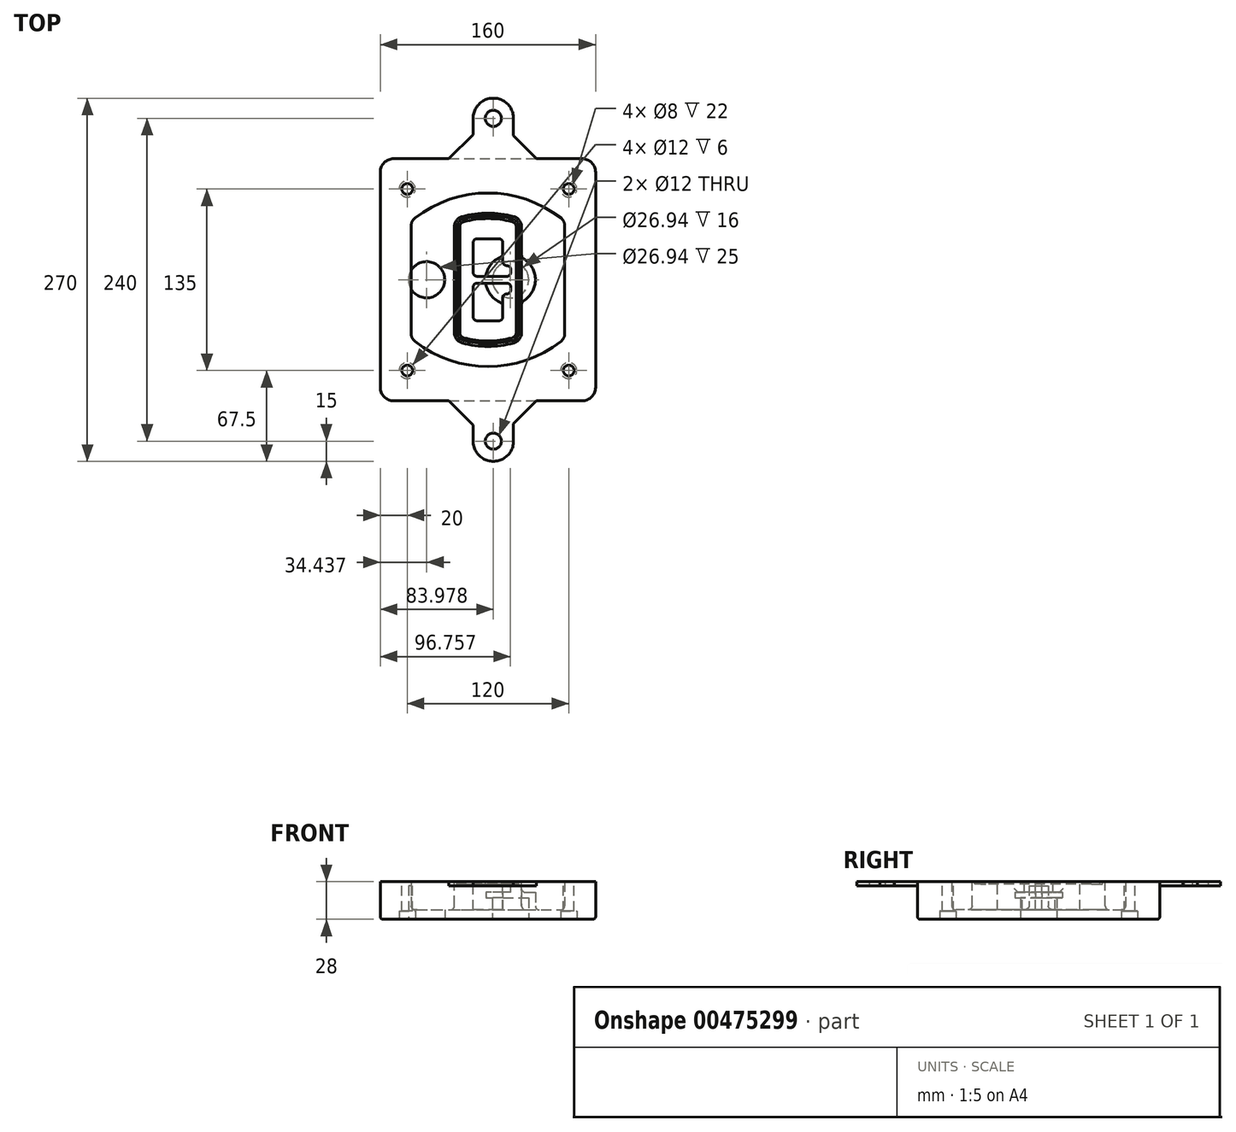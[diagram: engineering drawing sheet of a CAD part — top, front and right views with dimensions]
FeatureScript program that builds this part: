
annotation { "Feature Type Name" : "Feature", "Feature Type Description" : "" }
export const myFeature = defineFeature(function(context is Context, id is Id, definition is map)
    precondition{}
    {
        {
            var Q0;
            Q0=qCreatedBy(makeId("Top.planeOp"),FACE);
            var sketch = newSketch(context, id + "F0", { "sketchPlane" : qUnion([Q0])});
            skPoint(sketch, "E0.rect.middle", {"position": v(0, 0) * mm});
            skLineSegment(sketch, "E1.bottom", {"start": v(-70, -90) * mm, "end": v(70, -90) * mm});
            skLineSegment(sketch, "E1.top", {"start": v(-70, 90) * mm, "end": v(70, 90) * mm});
            skLineSegment(sketch, "E1.left", {"start": v(-80, -80) * mm, "end": v(-80, 80) * mm});
            skLineSegment(sketch, "E1.right", {"start": v(80, -80) * mm, "end": v(80, 80) * mm});
            skLineSegment(sketch, "E2", {"start": v(-80, 90) * mm, "end": v(80, -90) * mm, "construction": true});
            skLineSegment(sketch, "E3", {"start": v(80, 90) * mm, "end": v(-80, -90) * mm, "construction": true});
            skCircle(sketch, "E4", {"center": v(-60, 67.5) * mm, "radius": 4 * mm});
            skCircle(sketch, "E5", {"center": v(60, 67.5) * mm, "radius": 4 * mm});
            skCircle(sketch, "E6", {"center": v(60, -67.5) * mm, "radius": 4 * mm});
            skCircle(sketch, "E7", {"center": v(-60, -67.5) * mm, "radius": 4 * mm});
            skLineSegment(sketch, "E8", {"start": v(-60, 67.5) * mm, "end": v(60, 67.5) * mm, "construction": true});
            skLineSegment(sketch, "E9", {"start": v(60, 67.5) * mm, "end": v(60, -67.5) * mm, "construction": true});
            skLineSegment(sketch, "E10", {"start": v(60, -67.5) * mm, "end": v(-60, -67.5) * mm, "construction": true});
            skLineSegment(sketch, "E11", {"start": v(-60, -67.5) * mm, "end": v(-60, 67.5) * mm, "construction": true});
            skLineSegment(sketch, "E12", {"start": v(-60, 40.3) * mm, "end": v(-60, -40.3) * mm});
            skLineSegment(sketch, "E13", {"start": v(60, 40.3) * mm, "end": v(60, -40.3) * mm});
            skArc(sketch, "E14", {"start": v(56.15, 48.18) * mm, "mid": v(0, 67.5) * mm, "end": v(-56.15, 48.18) * mm});
            skArc(sketch, "E15", {"start": v(-56.15, -48.18) * mm, "mid": v(0, -67.5) * mm, "end": v(56.15, -48.18) * mm});
            skLineSegment(sketch, "E16", {"start": v(-60, 0) * mm, "end": v(60, 0) * mm, "construction": true});
            skPoint(sketch, "E17.visualSharp", {"position": v(-60, -45) * mm});
            skArc(sketch, "E17.filletArc", {"start": v(-60, -40.3) * mm, "mid": v(-58.99, -44.68) * mm, "end": v(-56.15, -48.18) * mm});
            skPoint(sketch, "E18.visualSharp", {"position": v(-60, 45) * mm});
            skArc(sketch, "E18.filletArc", {"start": v(-56.15, 48.18) * mm, "mid": v(-58.99, 44.68) * mm, "end": v(-60, 40.3) * mm});
            skPoint(sketch, "E19.visualSharp", {"position": v(60, 45) * mm});
            skArc(sketch, "E19.filletArc", {"start": v(60, 40.3) * mm, "mid": v(58.99, 44.68) * mm, "end": v(56.15, 48.18) * mm});
            skPoint(sketch, "E20.visualSharp", {"position": v(60, -45) * mm});
            skArc(sketch, "E20.filletArc", {"start": v(56.15, -48.18) * mm, "mid": v(58.99, -44.68) * mm, "end": v(60, -40.3) * mm});
            skPoint(sketch, "E21.visualSharp", {"position": v(-80, 90) * mm});
            skArc(sketch, "E21.filletArc", {"start": v(-70, 90) * mm, "mid": v(-77.07, 87.07) * mm, "end": v(-80, 80) * mm});
            skPoint(sketch, "E22.visualSharp", {"position": v(80, 90) * mm});
            skArc(sketch, "E22.filletArc", {"start": v(80, 80) * mm, "mid": v(77.07, 87.07) * mm, "end": v(70, 90) * mm});
            skPoint(sketch, "E23.visualSharp", {"position": v(80, -90) * mm});
            skArc(sketch, "E23.filletArc", {"start": v(70, -90) * mm, "mid": v(77.07, -87.07) * mm, "end": v(80, -80) * mm});
            skPoint(sketch, "E24.visualSharp", {"position": v(-80, -90) * mm});
            skArc(sketch, "E24.filletArc", {"start": v(-80, -80) * mm, "mid": v(-77.07, -87.07) * mm, "end": v(-70, -90) * mm});
            skArc(sketch, "E25.0", {"start": v(57, 40.3) * mm, "mid": v(56.3, 43.36) * mm, "end": v(54.3, 45.81) * mm});
            skLineSegment(sketch, "E25.1", {"start": v(57, 40.3) * mm, "end": v(57, -40.3) * mm});
            skArc(sketch, "E25.2", {"start": v(54.3, -45.81) * mm, "mid": v(56.3, -43.36) * mm, "end": v(57, -40.3) * mm});
            skArc(sketch, "E25.3", {"start": v(-54.3, -45.81) * mm, "mid": v(0, -64.5) * mm, "end": v(54.3, -45.81) * mm});
            skArc(sketch, "E25.4", {"start": v(-57, -40.3) * mm, "mid": v(-56.3, -43.36) * mm, "end": v(-54.3, -45.81) * mm});
            skArc(sketch, "E25.5", {"start": v(54.3, 45.81) * mm, "mid": v(0, 64.5) * mm, "end": v(-54.3, 45.81) * mm});
            skLineSegment(sketch, "E25.6", {"start": v(-57, 40.3) * mm, "end": v(-57, -40.3) * mm});
            skArc(sketch, "E25.7", {"start": v(-54.3, 45.81) * mm, "mid": v(-56.3, 43.36) * mm, "end": v(-57, 40.3) * mm});
            skArc(sketch, "E26.0", {"start": v(-58.62, 51.33) * mm, "mid": v(-62.58, 46.43) * mm, "end": v(-64, 40.3) * mm});
            skArc(sketch, "E26.1", {"start": v(58.62, 51.33) * mm, "mid": v(0, 71.5) * mm, "end": v(-58.62, 51.33) * mm});
            skArc(sketch, "E26.2", {"start": v(64, 40.3) * mm, "mid": v(62.58, 46.43) * mm, "end": v(58.62, 51.33) * mm});
            skLineSegment(sketch, "E26.3", {"start": v(64, 40.3) * mm, "end": v(64, -40.3) * mm});
            skArc(sketch, "E26.4", {"start": v(58.62, -51.33) * mm, "mid": v(62.58, -46.43) * mm, "end": v(64, -40.3) * mm});
            skLineSegment(sketch, "E26.5", {"start": v(-64, 40.3) * mm, "end": v(-64, -40.3) * mm});
            skArc(sketch, "E26.6", {"start": v(-58.62, -51.33) * mm, "mid": v(0, -71.5) * mm, "end": v(58.62, -51.33) * mm});
            skArc(sketch, "E26.7", {"start": v(-64, -40.3) * mm, "mid": v(-62.58, -46.43) * mm, "end": v(-58.62, -51.33) * mm});
            skSolve(sketch);
        }
        {
            var Q0;
            Q0=makeQuery(id+"F0.imprint","IMPRINT",FACE,{"disambiguationData":[TD([[makeQuery(id+"F0.imprint","IMPRINT",EDGE,{"derivedFrom":sQuery(id+"F0.wireOp",EDGE,"E1.bottom")}),1.0]])]});
            var Q1;
            Q1=makeQuery(id+"F0.imprint","IMPRINT",FACE,{"disambiguationData":[TD([[makeQuery(id+"F0.imprint","IMPRINT",EDGE,{"derivedFrom":sQuery(id+"F0.wireOp",EDGE,"E12")}),1.0]])]});
            var Q2;
            Q2=makeQuery(id+"F0.imprint","IMPRINT",FACE,{"disambiguationData":[TD([[makeQuery(id+"F0.imprint","IMPRINT",EDGE,{"derivedFrom":sQuery(id+"F0.wireOp",EDGE,"E25.0")}),1.0]])]});
            var Q3;
            Q3=makeQuery(id+"F0.imprint","IMPRINT",FACE,{"disambiguationData":[TD([[makeQuery(id+"F0.imprint","IMPRINT",EDGE,{"derivedFrom":sQuery(id+"F0.wireOp",EDGE,"E12")}),-1.0]])]});
            extrude(context, id + "F1", {"entities" : qUnion([Q0, Q1, Q2, Q3]), "oppositeDirection" : true, "depth" : 25 * mm});
        }
        {
            var Q0;
            Q0=makeQuery(id+"F0.imprint","IMPRINT",FACE,{"disambiguationData":[TD([[makeQuery(id+"F0.imprint","IMPRINT",EDGE,{"derivedFrom":sQuery(id+"F0.wireOp",EDGE,"E12")}),1.0]])]});
            extrude(context, id + "F2", {"entities" : qUnion([Q0]), "operationType" : NewBodyOperationType.ADD, "depth" : 3 * mm});
        }
        {
            var Q0;
            Q0=makeQuery(id+"F0.imprint","IMPRINT",FACE,{"disambiguationData":[TD([[makeQuery(id+"F0.imprint","IMPRINT",EDGE,{"derivedFrom":sQuery(id+"F0.wireOp",EDGE,"E25.0")}),1.0]])]});
            extrude(context, id + "F3", {"entities" : qUnion([Q0]), "operationType" : NewBodyOperationType.REMOVE, "oppositeDirection" : true, "depth" : 18 * mm});
        }
        {
            var Q0;
            Q0=makeQuery(id+"F2.opExtrude","CAP_FACE",FACE,{"disambiguationData":[OSD([sQuery(id+"F0.wireOp",EDGE,"E12"),sQuery(id+"F0.wireOp",EDGE,"E13"),sQuery(id+"F0.wireOp",EDGE,"E14"),sQuery(id+"F0.wireOp",EDGE,"E15"),sQuery(id+"F0.wireOp",EDGE,"E17.filletArc"),sQuery(id+"F0.wireOp",EDGE,"E18.filletArc"),sQuery(id+"F0.wireOp",EDGE,"E19.filletArc"),sQuery(id+"F0.wireOp",EDGE,"E20.filletArc"),sQuery(id+"F0.wireOp",EDGE,"E25.0"),sQuery(id+"F0.wireOp",EDGE,"E25.1"),sQuery(id+"F0.wireOp",EDGE,"E25.2"),sQuery(id+"F0.wireOp",EDGE,"E25.3"),sQuery(id+"F0.wireOp",EDGE,"E25.4"),sQuery(id+"F0.wireOp",EDGE,"E25.5"),sQuery(id+"F0.wireOp",EDGE,"E25.6"),sQuery(id+"F0.wireOp",EDGE,"E25.7")])],"isStart":false});
            var sketch = newSketch(context, id + "F4", { "sketchPlane" : qUnion([Q0])});
            skArc(sketch, "E27.0", {"start": v(-19.08, -46.97) * mm, "mid": v(0, -49.5) * mm, "end": v(19.08, -46.97) * mm});
            skArc(sketch, "E28.0", {"start": v(19.08, 46.97) * mm, "mid": v(0, 49.5) * mm, "end": v(-19.08, 46.97) * mm});
            skLineSegment(sketch, "E29", {"start": v(-25, 39.25) * mm, "end": v(-25, -39.25) * mm});
            skLineSegment(sketch, "E30", {"start": v(25, 39.25) * mm, "end": v(25, -39.25) * mm});
            skLineSegment(sketch, "E31", {"start": v(-25, 45.1) * mm, "end": v(25, 45.1) * mm, "construction": true});
            skLineSegment(sketch, "E32", {"start": v(-25, -45.1) * mm, "end": v(25, -45.1) * mm, "construction": true});
            skPoint(sketch, "E33.visualSharp", {"position": v(-25, 45.1) * mm});
            skArc(sketch, "E33.filletArc", {"start": v(-19.08, 46.97) * mm, "mid": v(-23.35, 44.11) * mm, "end": v(-25, 39.25) * mm});
            skPoint(sketch, "E34.visualSharp", {"position": v(25, 45.1) * mm});
            skArc(sketch, "E34.filletArc", {"start": v(25, 39.25) * mm, "mid": v(23.35, 44.11) * mm, "end": v(19.08, 46.97) * mm});
            skPoint(sketch, "E35.visualSharp", {"position": v(25, -45.1) * mm});
            skArc(sketch, "E35.filletArc", {"start": v(19.08, -46.97) * mm, "mid": v(23.35, -44.11) * mm, "end": v(25, -39.25) * mm});
            skPoint(sketch, "E36.visualSharp", {"position": v(-25, -45.1) * mm});
            skArc(sketch, "E36.filletArc", {"start": v(-25, -39.25) * mm, "mid": v(-23.35, -44.11) * mm, "end": v(-19.08, -46.97) * mm});
            skArc(sketch, "E37.0", {"start": v(54.3, 45.81) * mm, "mid": v(0, 64.5) * mm, "end": v(-54.3, 45.81) * mm});
            skArc(sketch, "E37.1", {"start": v(-54.3, 45.81) * mm, "mid": v(-56.3, 43.36) * mm, "end": v(-57, 40.3) * mm});
            skLineSegment(sketch, "E37.2", {"start": v(-57, 40.3) * mm, "end": v(-57, -40.3) * mm});
            skArc(sketch, "E37.3", {"start": v(-57, -40.3) * mm, "mid": v(-56.3, -43.36) * mm, "end": v(-54.3, -45.81) * mm});
            skArc(sketch, "E37.4", {"start": v(-54.3, -45.81) * mm, "mid": v(0, -64.5) * mm, "end": v(54.3, -45.81) * mm});
            skArc(sketch, "E37.5", {"start": v(54.3, -45.81) * mm, "mid": v(56.3, -43.36) * mm, "end": v(57, -40.3) * mm});
            skLineSegment(sketch, "E37.6", {"start": v(57, 40.3) * mm, "end": v(57, -40.3) * mm});
            skArc(sketch, "E37.7", {"start": v(57, 40.3) * mm, "mid": v(56.3, 43.36) * mm, "end": v(54.3, 45.81) * mm});
            skLineSegment(sketch, "E38.0", {"start": v(23, 39.25) * mm, "end": v(23, -39.25) * mm});
            skArc(sketch, "E38.1", {"start": v(18.56, -45.04) * mm, "mid": v(21.76, -42.9) * mm, "end": v(23, -39.25) * mm});
            skArc(sketch, "E38.2", {"start": v(-18.56, -45.04) * mm, "mid": v(0, -47.5) * mm, "end": v(18.56, -45.04) * mm});
            skArc(sketch, "E38.3", {"start": v(-23, -39.25) * mm, "mid": v(-21.76, -42.9) * mm, "end": v(-18.56, -45.04) * mm});
            skLineSegment(sketch, "E38.4", {"start": v(-23, 39.25) * mm, "end": v(-23, -39.25) * mm});
            skArc(sketch, "E38.5", {"start": v(23, 39.25) * mm, "mid": v(21.76, 42.9) * mm, "end": v(18.56, 45.04) * mm});
            skArc(sketch, "E38.6", {"start": v(-18.56, 45.04) * mm, "mid": v(-21.76, 42.9) * mm, "end": v(-23, 39.25) * mm});
            skArc(sketch, "E38.7", {"start": v(18.56, 45.04) * mm, "mid": v(0, 47.5) * mm, "end": v(-18.56, 45.04) * mm});
            skArc(sketch, "E39.0", {"start": v(21, 39.25) * mm, "mid": v(20.18, 41.68) * mm, "end": v(18.04, 43.1) * mm});
            skLineSegment(sketch, "E39.1", {"start": v(21, 39.25) * mm, "end": v(21, -39.25) * mm});
            skArc(sketch, "E39.2", {"start": v(18.04, -43.1) * mm, "mid": v(20.18, -41.68) * mm, "end": v(21, -39.25) * mm});
            skArc(sketch, "E39.3", {"start": v(-18.04, -43.1) * mm, "mid": v(0, -45.5) * mm, "end": v(18.04, -43.1) * mm});
            skArc(sketch, "E39.4", {"start": v(-21, -39.25) * mm, "mid": v(-20.18, -41.68) * mm, "end": v(-18.04, -43.1) * mm});
            skArc(sketch, "E39.5", {"start": v(18.04, 43.1) * mm, "mid": v(0, 45.5) * mm, "end": v(-18.04, 43.1) * mm});
            skLineSegment(sketch, "E39.6", {"start": v(-21, 39.25) * mm, "end": v(-21, -39.25) * mm});
            skArc(sketch, "E39.7", {"start": v(-18.04, 43.1) * mm, "mid": v(-20.18, 41.68) * mm, "end": v(-21, 39.25) * mm});
            skLineSegment(sketch, "E40", {"start": v(-25, 0) * mm, "end": v(25, 0) * mm, "construction": true});
            skLineSegment(sketch, "E41", {"start": v(-11, 5.5) * mm, "end": v(-11, 27.5) * mm});
            skLineSegment(sketch, "E42", {"start": v(-8, 30.5) * mm, "end": v(8, 30.5) * mm});
            skLineSegment(sketch, "E43", {"start": v(11, 27.5) * mm, "end": v(11, 13.5) * mm});
            skLineSegment(sketch, "E44", {"start": v(14, 10.5) * mm, "end": v(14, 10.5) * mm});
            skLineSegment(sketch, "E45", {"start": v(17, 7.5) * mm, "end": v(17, 5.5) * mm});
            skLineSegment(sketch, "E46", {"start": v(14, 2.5) * mm, "end": v(-8, 2.5) * mm});
            skPoint(sketch, "E47.visualSharp", {"position": v(-11, 30.5) * mm});
            skArc(sketch, "E47.filletArc", {"start": v(-8, 30.5) * mm, "mid": v(-10.12, 29.62) * mm, "end": v(-11, 27.5) * mm});
            skPoint(sketch, "E48.visualSharp", {"position": v(11, 30.5) * mm});
            skArc(sketch, "E48.filletArc", {"start": v(11, 27.5) * mm, "mid": v(10.12, 29.62) * mm, "end": v(8, 30.5) * mm});
            skPoint(sketch, "E49.visualSharp", {"position": v(11, 10.5) * mm});
            skArc(sketch, "E49.filletArc", {"start": v(11, 13.5) * mm, "mid": v(11.88, 11.38) * mm, "end": v(14, 10.5) * mm});
            skPoint(sketch, "E50.visualSharp", {"position": v(17, 10.5) * mm});
            skArc(sketch, "E50.filletArc", {"start": v(17, 7.5) * mm, "mid": v(16.12, 9.62) * mm, "end": v(14, 10.5) * mm});
            skPoint(sketch, "E51.visualSharp", {"position": v(17, 2.5) * mm});
            skArc(sketch, "E51.filletArc", {"start": v(14, 2.5) * mm, "mid": v(16.12, 3.38) * mm, "end": v(17, 5.5) * mm});
            skPoint(sketch, "E52.visualSharp", {"position": v(-11, 2.5) * mm});
            skArc(sketch, "E52.filletArc", {"start": v(-11, 5.5) * mm, "mid": v(-10.12, 3.38) * mm, "end": v(-8, 2.5) * mm});
            skLineSegment(sketch, "E53.0.MirrorCS", {"start": v(14, -2.5) * mm, "end": v(-8, -2.5) * mm});
            skArc(sketch, "E54.0.MirrorCS", {"start": v(-11, -5.5) * mm, "mid": v(-10.12, -3.38) * mm, "end": v(-8, -2.5) * mm});
            skLineSegment(sketch, "E55.0.MirrorCS", {"start": v(-11, -5.5) * mm, "end": v(-11, -27.5) * mm});
            skArc(sketch, "E56.0.MirrorCS", {"start": v(-8, -30.5) * mm, "mid": v(-10.12, -29.62) * mm, "end": v(-11, -27.5) * mm});
            skLineSegment(sketch, "E57.0.MirrorCS", {"start": v(-8, -30.5) * mm, "end": v(8, -30.5) * mm});
            skArc(sketch, "E58.0.MirrorCS", {"start": v(11, -27.5) * mm, "mid": v(10.12, -29.62) * mm, "end": v(8, -30.5) * mm});
            skLineSegment(sketch, "E59.0.MirrorCS", {"start": v(11, -27.5) * mm, "end": v(11, -13.5) * mm});
            skArc(sketch, "E60.0.MirrorCS", {"start": v(11, -13.5) * mm, "mid": v(11.88, -11.38) * mm, "end": v(14, -10.5) * mm});
            skArc(sketch, "E61.0.MirrorCS", {"start": v(17, -7.5) * mm, "mid": v(16.12, -9.62) * mm, "end": v(14, -10.5) * mm});
            skLineSegment(sketch, "E62.0.MirrorCS", {"start": v(17, -7.5) * mm, "end": v(17, -5.5) * mm});
            skArc(sketch, "E63.0.MirrorCS", {"start": v(14, -2.5) * mm, "mid": v(16.12, -3.38) * mm, "end": v(17, -5.5) * mm});
            skSolve(sketch);
        }
        {
            var Q0;
            Q0=makeQuery(id+"F4.imprint","IMPRINT",FACE,{"disambiguationData":[TD([[makeQuery(id+"F4.imprint","IMPRINT",EDGE,{"derivedFrom":sQuery(id+"F4.wireOp",EDGE,"E27.0")}),1.0]])]});
            var Q1;
            Q1=makeQuery(id+"F4.imprint","IMPRINT",FACE,{"disambiguationData":[TD([[makeQuery(id+"F4.imprint","IMPRINT",EDGE,{"derivedFrom":sQuery(id+"F4.wireOp",EDGE,"E38.0")}),-1.0]])]});
            var Q2;
            Q2=makeQuery(id+"F4.imprint","IMPRINT",FACE,{"disambiguationData":[TD([[makeQuery(id+"F4.imprint","IMPRINT",EDGE,{"derivedFrom":sQuery(id+"F4.wireOp",EDGE,"E39.0")}),1.0]])]});
            extrude(context, id + "F5", {"entities" : qUnion([Q0, Q1, Q2]), "operationType" : NewBodyOperationType.ADD, "endBound" : BoundingType.UP_TO_NEXT, "oppositeDirection" : true, "depth" : 25 * mm});
        }
        {
            var Q0;
            Q0=makeQuery(id+"F4.imprint","IMPRINT",FACE,{"disambiguationData":[TD([[makeQuery(id+"F4.imprint","IMPRINT",EDGE,{"derivedFrom":sQuery(id+"F4.wireOp",EDGE,"E38.0")}),-1.0]])]});
            extrude(context, id + "F6", {"entities" : qUnion([Q0]), "operationType" : NewBodyOperationType.REMOVE, "oppositeDirection" : true, "depth" : 2 * mm});
        }
        {
            var Q0;
            Q0=makeQuery(id+"F1.opExtrude","CAP_FACE",FACE,{"disambiguationData":[OSD([sQuery(id+"F0.wireOp",EDGE,"E1.bottom"),sQuery(id+"F0.wireOp",EDGE,"E1.top"),sQuery(id+"F0.wireOp",EDGE,"E1.left"),sQuery(id+"F0.wireOp",EDGE,"E1.right"),sQuery(id+"F0.wireOp",EDGE,"E4"),sQuery(id+"F0.wireOp",EDGE,"E5"),sQuery(id+"F0.wireOp",EDGE,"E6"),sQuery(id+"F0.wireOp",EDGE,"E7"),sQuery(id+"F0.wireOp",EDGE,"E21.filletArc"),sQuery(id+"F0.wireOp",EDGE,"E22.filletArc"),sQuery(id+"F0.wireOp",EDGE,"E23.filletArc"),sQuery(id+"F0.wireOp",EDGE,"E24.filletArc")])],"isStart":false});
            var sketch = newSketch(context, id + "F7", { "sketchPlane" : qUnion([Q0])});
            skCircle(sketch, "E64", {"center": v(16.76, 0) * mm, "radius": 13.47 * mm});
            skCircle(sketch, "E65", {"center": v(-45.56, 0) * mm, "radius": 13.47 * mm});
            skLineSegment(sketch, "E66", {"start": v(80, 0) * mm, "end": v(-80, 0) * mm});
            skCircle(sketch, "E67", {"center": v(16.76, 0) * mm, "radius": 18.47 * mm});
            skCircle(sketch, "E68", {"center": v(60, -67.5) * mm, "radius": 6 * mm});
            skCircle(sketch, "E69", {"center": v(-60, -67.5) * mm, "radius": 6 * mm});
            skCircle(sketch, "E70", {"center": v(-60, 67.5) * mm, "radius": 6 * mm});
            skCircle(sketch, "E71", {"center": v(60, 67.5) * mm, "radius": 6 * mm});
            skSolve(sketch);
        }
        {
            var Q0;
            {var subQ1=sQuery(id+"F7.wireOp",EDGE,"E66");var subQ4=sQuery(id+"F7.wireOp",EDGE,"E64");var subQ6=makeQuery(id+"F7.imprint","INTERSECT",VERTEX,{"disambiguationData":[OD(0.0)],"derivedFrom":[subQ4,subQ1]});Q0=makeQuery(id+"F7.imprint","IMPRINT",FACE,{"disambiguationData":[TD([[makeQuery(id+"F7.imprint","IMPRINT",EDGE,{"disambiguationData":[TD([[subQ6,-1.0]])],"derivedFrom":subQ4}),-1.0]])]});}
            var Q1;
            {var subQ0=sQuery(id+"F7.wireOp",EDGE,"E66");var subQ1=sQuery(id+"F7.wireOp",EDGE,"E64");var subQ3=makeQuery(id+"F7.imprint","INTERSECT",VERTEX,{"disambiguationData":[OD(0.0)],"derivedFrom":[subQ1,subQ0]});Q1=makeQuery(id+"F7.imprint","IMPRINT",FACE,{"disambiguationData":[TD([[makeQuery(id+"F7.imprint","IMPRINT",EDGE,{"disambiguationData":[TD([[subQ3,-1.0]])],"derivedFrom":subQ1}),1.0]])]});}
            var Q2;
            {var subQ0=sQuery(id+"F7.wireOp",EDGE,"E66");var subQ1=sQuery(id+"F7.wireOp",EDGE,"E64");var subQ3=makeQuery(id+"F7.imprint","INTERSECT",VERTEX,{"disambiguationData":[OD(0.0)],"derivedFrom":[subQ1,subQ0]});Q2=makeQuery(id+"F7.imprint","IMPRINT",FACE,{"disambiguationData":[TD([[makeQuery(id+"F7.imprint","IMPRINT",EDGE,{"disambiguationData":[TD([[subQ3,1.0]])],"derivedFrom":subQ1}),1.0]])]});}
            var Q3;
            {var subQ1=sQuery(id+"F7.wireOp",EDGE,"E66");var subQ4=sQuery(id+"F7.wireOp",EDGE,"E64");var subQ6=makeQuery(id+"F7.imprint","INTERSECT",VERTEX,{"disambiguationData":[OD(0.0)],"derivedFrom":[subQ4,subQ1]});Q3=makeQuery(id+"F7.imprint","IMPRINT",FACE,{"disambiguationData":[TD([[makeQuery(id+"F7.imprint","IMPRINT",EDGE,{"disambiguationData":[TD([[subQ6,1.0]])],"derivedFrom":subQ4}),-1.0]])]});}
            extrude(context, id + "F8", {"entities" : qUnion([Q0, Q1, Q2, Q3]), "operationType" : NewBodyOperationType.ADD, "oppositeDirection" : true, "depth" : 20 * mm});
        }
        {
            var Q0;
            {var subQ0=sQuery(id+"F7.wireOp",EDGE,"E66");var subQ1=sQuery(id+"F7.wireOp",EDGE,"E64");var subQ3=makeQuery(id+"F7.imprint","INTERSECT",VERTEX,{"disambiguationData":[OD(0.0)],"derivedFrom":[subQ1,subQ0]});Q0=makeQuery(id+"F7.imprint","IMPRINT",FACE,{"disambiguationData":[TD([[makeQuery(id+"F7.imprint","IMPRINT",EDGE,{"disambiguationData":[TD([[subQ3,-1.0]])],"derivedFrom":subQ1}),1.0]])]});}
            var Q1;
            {var subQ0=sQuery(id+"F7.wireOp",EDGE,"E66");var subQ1=sQuery(id+"F7.wireOp",EDGE,"E64");var subQ3=makeQuery(id+"F7.imprint","INTERSECT",VERTEX,{"disambiguationData":[OD(0.0)],"derivedFrom":[subQ1,subQ0]});Q1=makeQuery(id+"F7.imprint","IMPRINT",FACE,{"disambiguationData":[TD([[makeQuery(id+"F7.imprint","IMPRINT",EDGE,{"disambiguationData":[TD([[subQ3,1.0]])],"derivedFrom":subQ1}),1.0]])]});}
            extrude(context, id + "F9", {"entities" : qUnion([Q0, Q1]), "operationType" : NewBodyOperationType.REMOVE, "oppositeDirection" : true, "depth" : 16 * mm});
        }
        {
            var Q0;
            {var subQ0=sQuery(id+"F7.wireOp",EDGE,"E66");var subQ1=sQuery(id+"F7.wireOp",EDGE,"E65");var subQ3=makeQuery(id+"F7.imprint","INTERSECT",VERTEX,{"disambiguationData":[OD(0.0)],"derivedFrom":[subQ1,subQ0]});Q0=makeQuery(id+"F7.imprint","IMPRINT",FACE,{"disambiguationData":[TD([[makeQuery(id+"F7.imprint","IMPRINT",EDGE,{"disambiguationData":[TD([[subQ3,-1.0]])],"derivedFrom":subQ1}),1.0]])]});}
            var Q1;
            {var subQ0=sQuery(id+"F7.wireOp",EDGE,"E66");var subQ1=sQuery(id+"F7.wireOp",EDGE,"E65");var subQ3=makeQuery(id+"F7.imprint","INTERSECT",VERTEX,{"disambiguationData":[OD(0.0)],"derivedFrom":[subQ1,subQ0]});Q1=makeQuery(id+"F7.imprint","IMPRINT",FACE,{"disambiguationData":[TD([[makeQuery(id+"F7.imprint","IMPRINT",EDGE,{"disambiguationData":[TD([[subQ3,1.0]])],"derivedFrom":subQ1}),1.0]])]});}
            extrude(context, id + "F10", {"entities" : qUnion([Q0, Q1]), "operationType" : NewBodyOperationType.REMOVE, "oppositeDirection" : true, "depth" : 25 * mm});
        }
        {
            var Q0;
            Q0=makeQuery(id+"F7.imprint","IMPRINT",FACE,{"disambiguationData":[TD([[makeQuery(id+"F7.imprint","IMPRINT",EDGE,{"derivedFrom":sQuery(id+"F7.wireOp",EDGE,"E68")}),1.0]])]});
            var Q1;
            Q1=makeQuery(id+"F7.imprint","IMPRINT",FACE,{"disambiguationData":[TD([[makeQuery(id+"F7.imprint","IMPRINT",EDGE,{"derivedFrom":makeQuery(id+"F1.opExtrude","CAP_EDGE",EDGE,{"disambiguationData":[OSD([sQuery(id+"F0.wireOp",EDGE,"E5")])],"isStart":false})}),-1.0]])]});
            var Q2;
            Q2=makeQuery(id+"F7.imprint","IMPRINT",FACE,{"disambiguationData":[TD([[makeQuery(id+"F7.imprint","IMPRINT",EDGE,{"derivedFrom":sQuery(id+"F7.wireOp",EDGE,"E69")}),1.0]])]});
            var Q3;
            Q3=makeQuery(id+"F7.imprint","IMPRINT",FACE,{"disambiguationData":[TD([[makeQuery(id+"F7.imprint","IMPRINT",EDGE,{"derivedFrom":makeQuery(id+"F1.opExtrude","CAP_EDGE",EDGE,{"disambiguationData":[OSD([sQuery(id+"F0.wireOp",EDGE,"E4")])],"isStart":false})}),-1.0]])]});
            var Q4;
            Q4=makeQuery(id+"F7.imprint","IMPRINT",FACE,{"disambiguationData":[TD([[makeQuery(id+"F7.imprint","IMPRINT",EDGE,{"derivedFrom":sQuery(id+"F7.wireOp",EDGE,"E70")}),1.0]])]});
            var Q5;
            Q5=makeQuery(id+"F7.imprint","IMPRINT",FACE,{"disambiguationData":[TD([[makeQuery(id+"F7.imprint","IMPRINT",EDGE,{"derivedFrom":makeQuery(id+"F1.opExtrude","CAP_EDGE",EDGE,{"disambiguationData":[OSD([sQuery(id+"F0.wireOp",EDGE,"E7")])],"isStart":false})}),-1.0]])]});
            var Q6;
            Q6=makeQuery(id+"F7.imprint","IMPRINT",FACE,{"disambiguationData":[TD([[makeQuery(id+"F7.imprint","IMPRINT",EDGE,{"derivedFrom":sQuery(id+"F7.wireOp",EDGE,"E71")}),1.0]])]});
            var Q7;
            Q7=makeQuery(id+"F7.imprint","IMPRINT",FACE,{"disambiguationData":[TD([[makeQuery(id+"F7.imprint","IMPRINT",EDGE,{"derivedFrom":makeQuery(id+"F1.opExtrude","CAP_EDGE",EDGE,{"disambiguationData":[OSD([sQuery(id+"F0.wireOp",EDGE,"E6")])],"isStart":false})}),-1.0]])]});
            extrude(context, id + "F11", {"entities" : qUnion([Q0, Q1, Q2, Q3, Q4, Q5, Q6, Q7]), "operationType" : NewBodyOperationType.REMOVE, "oppositeDirection" : true, "depth" : 6 * mm});
        }
        {
            var Q0;
            Q0=makeQuery(id+"F9.boolean.opBoolean","COPY",FACE,{"derivedFrom":makeQuery(id+"F9.opExtrude","CAP_FACE",FACE,{"disambiguationData":[OSD([sQuery(id+"F7.wireOp",EDGE,"E64")])],"isStart":false})});
            var sketch = newSketch(context, id + "F12", { "sketchPlane" : qUnion([Q0])});
            skArc(sketch, "E72.0", {"start": v(11, 17.55) * mm, "mid": v(2.57, 11.82) * mm, "end": v(-1.54, 2.5) * mm});
            skArc(sketch, "E72.1", {"start": v(-1.54, -2.5) * mm, "mid": v(2.57, -11.82) * mm, "end": v(11, -17.55) * mm});
            skLineSegment(sketch, "E73", {"start": v(-1.54, -2.5) * mm, "end": v(14, -2.5) * mm});
            skLineSegment(sketch, "E74.0", {"start": v(14, 2.5) * mm, "end": v(-1.54, 2.5) * mm});
            skArc(sketch, "E74.1", {"start": v(14, 2.5) * mm, "mid": v(16.12, 3.38) * mm, "end": v(17, 5.5) * mm});
            skLineSegment(sketch, "E74.2", {"start": v(17, 7.5) * mm, "end": v(17, 5.5) * mm});
            skArc(sketch, "E74.3", {"start": v(17, 7.5) * mm, "mid": v(16.12, 9.62) * mm, "end": v(14, 10.5) * mm});
            skArc(sketch, "E74.4", {"start": v(11, 13.5) * mm, "mid": v(11.88, 11.38) * mm, "end": v(14, 10.5) * mm});
            skLineSegment(sketch, "E74.5", {"start": v(11, 17.55) * mm, "end": v(11, 13.5) * mm});
            skLineSegment(sketch, "E74.7", {"start": v(14, -2.5) * mm, "end": v(-1.54, -2.5) * mm});
            skArc(sketch, "E74.8", {"start": v(14, -2.5) * mm, "mid": v(16.12, -3.38) * mm, "end": v(17, -5.5) * mm});
            skLineSegment(sketch, "E74.9", {"start": v(17, -7.5) * mm, "end": v(17, -5.5) * mm});
            skArc(sketch, "E74.10", {"start": v(17, -7.5) * mm, "mid": v(16.12, -9.62) * mm, "end": v(14, -10.5) * mm});
            skArc(sketch, "E74.11", {"start": v(11, -13.5) * mm, "mid": v(11.88, -11.38) * mm, "end": v(14, -10.5) * mm});
            skLineSegment(sketch, "E74.12", {"start": v(11, -17.55) * mm, "end": v(11, -13.5) * mm});
            skPoint(sketch, "E75.orphan", {"position": v(11, -27.5) * mm});
            skPoint(sketch, "E76.orphan", {"position": v(-8, -2.5) * mm});
            skPoint(sketch, "E77.orphan", {"position": v(-8, 2.5) * mm});
            skPoint(sketch, "E78.orphan", {"position": v(11, 27.5) * mm});
            skSolve(sketch);
        }
        {
            var Q0;
            {var subQ7=sQuery(id+"F12.wireOp",EDGE,"E72.0");var subQ14=sQuery(id+"F12.wireOp",EDGE,"E72.1");var subQ16=sQuery(id+"F12.wireOp",EDGE,"E74.1");var subQ18=sQuery(id+"F12.wireOp",EDGE,"E74.8");Q0=qUnion([makeQuery(id+"F12.imprint","IMPRINT",FACE,{"disambiguationData":[TD([[makeQuery(id+"F12.imprint","IMPRINT",EDGE,{"derivedFrom":subQ7}),1.0]])]}),makeQuery(id+"F12.imprint","IMPRINT",FACE,{"disambiguationData":[TD([[makeQuery(id+"F12.imprint","IMPRINT",EDGE,{"derivedFrom":subQ14}),1.0]])]}),makeQuery(id+"F12.imprint","IMPRINT",FACE,{"disambiguationData":[TD([[makeQuery(id+"F12.imprint","IMPRINT",EDGE,{"derivedFrom":subQ16}),1.0]])]}),makeQuery(id+"F12.imprint","IMPRINT",FACE,{"disambiguationData":[TD([[makeQuery(id+"F12.imprint","IMPRINT",EDGE,{"derivedFrom":subQ18}),-1.0]])]})]);}
            var Q1;
            Q1=makeQuery(id+"F5.boolean.opBoolean","SPLIT",FACE,{"disambiguationData":[TD([makeQuery(id+"F5.opExtrude","SWEPT_FACE",FACE,{"disambiguationData":[OSD([sQuery(id+"F4.wireOp",EDGE,"E41")])]})])],"derivedFrom":makeQuery(id+"F3.boolean.opBoolean","COPY",FACE,{"derivedFrom":makeQuery(id+"F3.opExtrude","CAP_FACE",FACE,{"disambiguationData":[OSD([sQuery(id+"F0.wireOp",EDGE,"E25.0"),sQuery(id+"F0.wireOp",EDGE,"E25.1"),sQuery(id+"F0.wireOp",EDGE,"E25.2"),sQuery(id+"F0.wireOp",EDGE,"E25.3"),sQuery(id+"F0.wireOp",EDGE,"E25.4"),sQuery(id+"F0.wireOp",EDGE,"E25.5"),sQuery(id+"F0.wireOp",EDGE,"E25.6"),sQuery(id+"F0.wireOp",EDGE,"E25.7")])],"isStart":false})})});
            extrude(context, id + "F13", {"entities" : qUnion([Q0]), "operationType" : NewBodyOperationType.REMOVE, "endBound" : BoundingType.UP_TO_SURFACE, "endBoundEntityFace" : qUnion([Q1]), "depth" : 25 * mm});
        }
        {
            var Q0;
            Q0=makeQuery(id+"F3.boolean.opBoolean","COPY",EDGE,{"derivedFrom":makeQuery(id+"F3.opExtrude","CAP_EDGE",EDGE,{"disambiguationData":[OSD([sQuery(id+"F0.wireOp",EDGE,"E25.6")])],"isStart":false})});
            var Q1;
            Q1=makeQuery(id+"F8.boolean.opBoolean","INTERSECT",EDGE,{"derivedFrom":[makeQuery(id+"F5.opExtrude","SWEPT_FACE",FACE,{"disambiguationData":[OSD([sQuery(id+"F4.wireOp",EDGE,"E30")])]}),makeQuery(id+"F8.opExtrude","CAP_FACE",FACE,{"disambiguationData":[OSD([sQuery(id+"F7.wireOp",EDGE,"E67")])],"isStart":false})]});
            var Q2;
            Q2=makeQuery(id+"F8.boolean.opBoolean","INTERSECT",EDGE,{"disambiguationData":[OD(1.0)],"derivedFrom":[makeQuery(id+"F5.opExtrude","SWEPT_FACE",FACE,{"disambiguationData":[OSD([sQuery(id+"F4.wireOp",EDGE,"E30")])]}),makeQuery(id+"F8.opExtrude","SWEPT_FACE",FACE,{"disambiguationData":[OSD([sQuery(id+"F7.wireOp",EDGE,"E67")])]})]});
            var Q3;
            {var subQ0=sQuery(id+"F4.wireOp",EDGE,"E30");Q3=makeQuery(id+"F8.boolean.opBoolean","SPLIT",EDGE,{"disambiguationData":[TD([makeQuery(id+"F5.opExtrude","SWEPT_FACE",FACE,{"disambiguationData":[OSD([sQuery(id+"F4.wireOp",EDGE,"E35.filletArc")])]})])],"derivedFrom":makeQuery(id+"F5.opExtrude","CAP_EDGE",EDGE,{"disambiguationData":[OSD([subQ0])],"isStart":false})});}
            var Q4;
            {var subQ0=sQuery(id+"F0.wireOp",EDGE,"E25.7");var subQ1=sQuery(id+"F0.wireOp",EDGE,"E25.1");var subQ2=sQuery(id+"F0.wireOp",EDGE,"E25.6");var subQ3=sQuery(id+"F0.wireOp",EDGE,"E25.5");var subQ4=sQuery(id+"F0.wireOp",EDGE,"E25.4");var subQ5=sQuery(id+"F0.wireOp",EDGE,"E25.0");var subQ6=sQuery(id+"F0.wireOp",EDGE,"E25.2");var subQ7=sQuery(id+"F0.wireOp",EDGE,"E25.3");Q4=makeQuery(id+"F8.boolean.opBoolean","INTERSECT",EDGE,{"derivedFrom":[makeQuery(id+"F5.boolean.opBoolean","SPLIT",FACE,{"disambiguationData":[TD([makeQuery(id+"F2.opExtrude","SWEPT_FACE",FACE,{"disambiguationData":[OSD([subQ5])]})])],"derivedFrom":makeQuery(id+"F3.boolean.opBoolean","COPY",FACE,{"derivedFrom":makeQuery(id+"F3.opExtrude","CAP_FACE",FACE,{"disambiguationData":[OSD([subQ5,subQ1,subQ6,subQ7,subQ4,subQ3,subQ2,subQ0])],"isStart":false})})}),makeQuery(id+"F8.opExtrude","SWEPT_FACE",FACE,{"disambiguationData":[OSD([sQuery(id+"F7.wireOp",EDGE,"E67")])]})]});}
            var Q5;
            Q5=makeQuery(id+"F8.boolean.opBoolean","INTERSECT",EDGE,{"disambiguationData":[OD(0.0)],"derivedFrom":[makeQuery(id+"F5.opExtrude","SWEPT_FACE",FACE,{"disambiguationData":[OSD([sQuery(id+"F4.wireOp",EDGE,"E30")])]}),makeQuery(id+"F8.opExtrude","SWEPT_FACE",FACE,{"disambiguationData":[OSD([sQuery(id+"F7.wireOp",EDGE,"E67")])]})]});
            fillet(context, id + "F14", {"entities" : qUnion([Q0, Q1, Q2, Q3, Q4, Q5]), "radius" : 3 * mm, "tangentPropagation" : true, "allowEdgeOverflow" : false});
        }
        {
            var Q0;
            Q0=makeQuery(id+"F1.opExtrude","CAP_EDGE",EDGE,{"disambiguationData":[OSD([sQuery(id+"F0.wireOp",EDGE,"E1.bottom")])],"isStart":false});
            fillet(context, id + "F15", {"entities" : qUnion([Q0]), "radius" : 2 * mm, "tangentPropagation" : true, "allowEdgeOverflow" : false});
        }
        {
            var Q0;
            {var subQ0=sQuery(id+"F0.wireOp",EDGE,"E21.filletArc");var subQ1=sQuery(id+"F0.wireOp",EDGE,"E7");var subQ2=sQuery(id+"F0.wireOp",EDGE,"E6");var subQ3=sQuery(id+"F0.wireOp",EDGE,"E5");var subQ4=sQuery(id+"F0.wireOp",EDGE,"E4");var subQ5=sQuery(id+"F0.wireOp",EDGE,"E22.filletArc");var subQ6=sQuery(id+"F0.wireOp",EDGE,"E1.bottom");var subQ7=sQuery(id+"F0.wireOp",EDGE,"E1.right");var subQ8=sQuery(id+"F0.wireOp",EDGE,"E1.top");var subQ9=sQuery(id+"F0.wireOp",EDGE,"E1.left");var subQ10=sQuery(id+"F0.wireOp",EDGE,"E23.filletArc");var subQ11=sQuery(id+"F0.wireOp",EDGE,"E24.filletArc");Q0=makeQuery(id+"F2.boolean.opBoolean","SPLIT",FACE,{"disambiguationData":[TD([makeQuery(id+"F1.opExtrude","SWEPT_FACE",FACE,{"disambiguationData":[OSD([subQ6])]})])],"derivedFrom":makeQuery(id+"F1.opExtrude","CAP_FACE",FACE,{"disambiguationData":[OSD([subQ6,subQ8,subQ9,subQ7,subQ4,subQ3,subQ2,subQ1,subQ0,subQ5,subQ10,subQ11])],"isStart":true})});}
            var sketch = newSketch(context, id + "F16", { "sketchPlane" : qUnion([Q0])});
            skLineSegment(sketch, "E79.0.0", {"start": v(70, 90) * mm, "end": v(-70, 90) * mm});
            skArc(sketch, "E79.0.1", {"start": v(-70, 90) * mm, "mid": v(-77.07, 87.07) * mm, "end": v(-80, 80) * mm});
            skLineSegment(sketch, "E79.0.2", {"start": v(-80, 80) * mm, "end": v(-80, -80) * mm});
            skArc(sketch, "E79.0.3", {"start": v(-80, -80) * mm, "mid": v(-77.07, -87.07) * mm, "end": v(-70, -90) * mm});
            skLineSegment(sketch, "E79.0.4", {"start": v(-70, -90) * mm, "end": v(70, -90) * mm});
            skArc(sketch, "E79.0.5", {"start": v(70, -90) * mm, "mid": v(77.07, -87.07) * mm, "end": v(80, -80) * mm});
            skLineSegment(sketch, "E79.0.6", {"start": v(80, -80) * mm, "end": v(80, 80) * mm});
            skArc(sketch, "E79.0.7", {"start": v(80, 80) * mm, "mid": v(77.07, 87.07) * mm, "end": v(70, 90) * mm});
            skLineSegment(sketch, "E80", {"start": v(-29.02, 90) * mm, "end": v(-11.02, 108) * mm});
            skLineSegment(sketch, "E81", {"start": v(-11.02, 108) * mm, "end": v(-11.02, 120) * mm});
            skLineSegment(sketch, "E82", {"start": v(18.85, 107.17) * mm, "end": v(18.85, 118.02) * mm});
            skArc(sketch, "E83", {"start": v(18.85, 118.02) * mm, "mid": v(4.97, 134.97) * mm, "end": v(-11.02, 120) * mm});
            skCircle(sketch, "E84", {"center": v(3.98, 120) * mm, "radius": 6 * mm});
            skLineSegment(sketch, "E85", {"start": v(18.85, 107.17) * mm, "end": v(36.01, 90) * mm});
            skLineSegment(sketch, "E86", {"start": v(3.98, 120) * mm, "end": v(3.98, 90) * mm, "construction": true});
            skLineSegment(sketch, "E87", {"start": v(-80, 0) * mm, "end": v(80, 0) * mm, "construction": true});
            skLineSegment(sketch, "E88.MirrorCS", {"start": v(18.85, -107.17) * mm, "end": v(18.85, -118.02) * mm});
            skLineSegment(sketch, "E89.MirrorCS", {"start": v(18.85, -107.17) * mm, "end": v(36.01, -90) * mm});
            skArc(sketch, "E90.MirrorCS", {"start": v(18.85, -118.02) * mm, "mid": v(4.97, -134.97) * mm, "end": v(-11.02, -120) * mm});
            skLineSegment(sketch, "E91.MirrorCS", {"start": v(-11.02, -108) * mm, "end": v(-11.02, -120) * mm});
            skLineSegment(sketch, "E92.MirrorCS", {"start": v(-29.02, -90) * mm, "end": v(-11.02, -108) * mm});
            skLineSegment(sketch, "E93.MirrorCS", {"start": v(3.98, -120) * mm, "end": v(3.98, -90) * mm, "construction": true});
            skCircle(sketch, "E94.MirrorC", {"center": v(3.98, -120) * mm, "radius": 6 * mm});
            skSolve(sketch);
        }
        {
            var Q0;
            {var subQ0=sQuery(id+"F16.wireOp",EDGE,"E80");Q0=makeQuery(id+"F16.imprint","IMPRINT",FACE,{"disambiguationData":[TD([[makeQuery(id+"F16.imprint","IMPRINT",EDGE,{"derivedFrom":subQ0}),-1.0]])]});}
            var Q1;
            {var subQ0=sQuery(id+"F16.wireOp",EDGE,"E89.MirrorCS");Q1=makeQuery(id+"F16.imprint","IMPRINT",FACE,{"disambiguationData":[TD([[makeQuery(id+"F16.imprint","IMPRINT",EDGE,{"derivedFrom":subQ0}),1.0]])]});}
            var Q2;
            {var subQ1=sQuery(id+"F16.wireOp",EDGE,"E79.0.1");Q2=makeQuery(id+"F16.imprint","IMPRINT",FACE,{"disambiguationData":[TD([[makeQuery(id+"F16.imprint","IMPRINT",EDGE,{"derivedFrom":subQ1}),1.0]])]});}
            var Q3;
            Q3=makeQuery(id+"F2.opExtrude","CAP_FACE",FACE,{"disambiguationData":[OSD([sQuery(id+"F0.wireOp",EDGE,"E12"),sQuery(id+"F0.wireOp",EDGE,"E13"),sQuery(id+"F0.wireOp",EDGE,"E14"),sQuery(id+"F0.wireOp",EDGE,"E15"),sQuery(id+"F0.wireOp",EDGE,"E17.filletArc"),sQuery(id+"F0.wireOp",EDGE,"E18.filletArc"),sQuery(id+"F0.wireOp",EDGE,"E19.filletArc"),sQuery(id+"F0.wireOp",EDGE,"E20.filletArc"),sQuery(id+"F0.wireOp",EDGE,"E25.0"),sQuery(id+"F0.wireOp",EDGE,"E25.1"),sQuery(id+"F0.wireOp",EDGE,"E25.2"),sQuery(id+"F0.wireOp",EDGE,"E25.3"),sQuery(id+"F0.wireOp",EDGE,"E25.4"),sQuery(id+"F0.wireOp",EDGE,"E25.5"),sQuery(id+"F0.wireOp",EDGE,"E25.6"),sQuery(id+"F0.wireOp",EDGE,"E25.7")])],"isStart":false});
            extrude(context, id + "F17", {"entities" : qUnion([Q0, Q1, Q2]), "operationType" : NewBodyOperationType.ADD, "endBound" : BoundingType.UP_TO_SURFACE, "endBoundEntityFace" : qUnion([Q3]), "depth" : 25 * mm});
        }
    });
